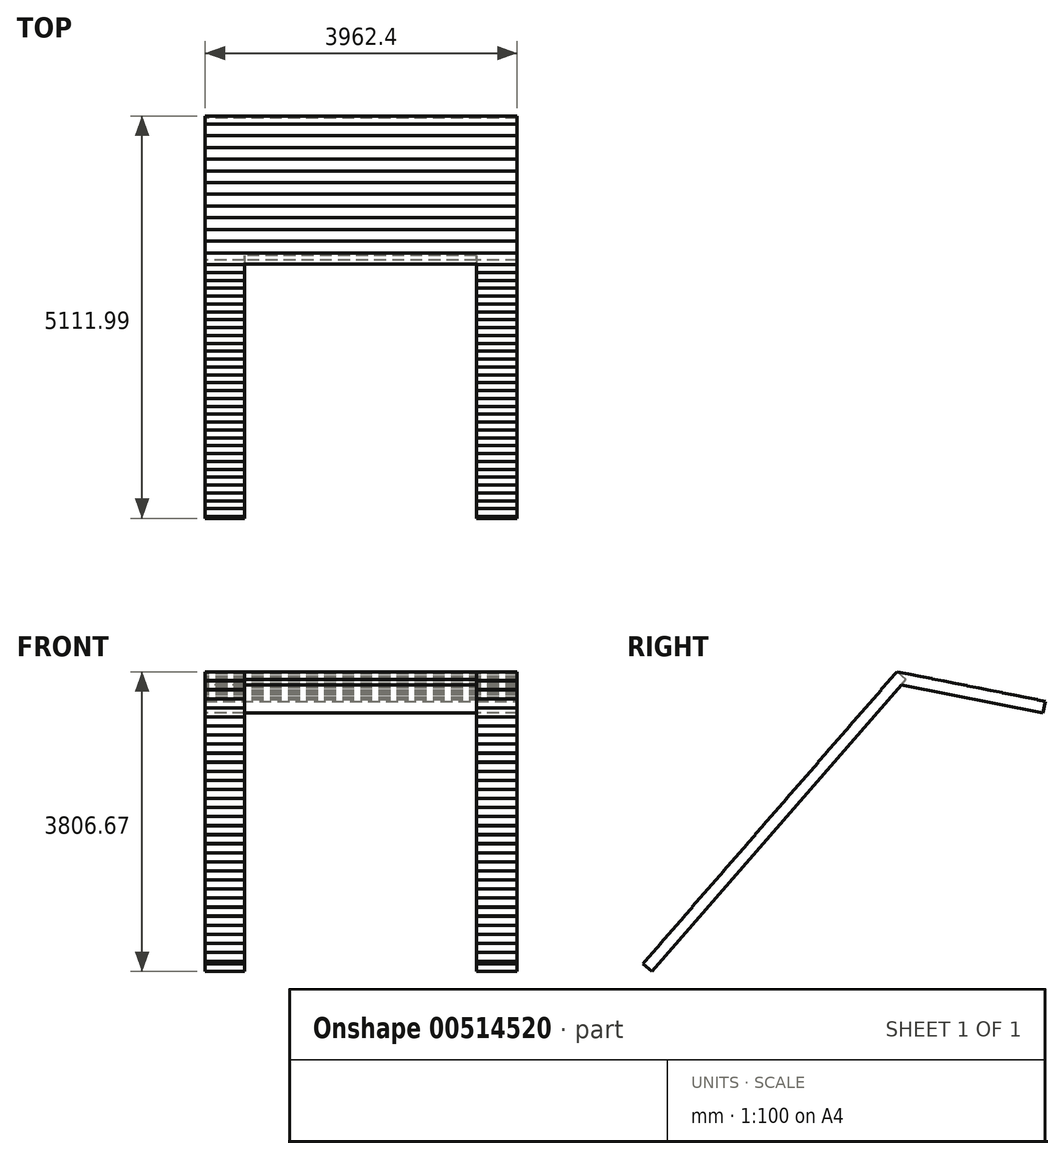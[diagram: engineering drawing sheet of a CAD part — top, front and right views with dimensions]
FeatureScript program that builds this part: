
annotation { "Feature Type Name" : "Feature", "Feature Type Description" : "" }
export const myFeature = defineFeature(function(context is Context, id is Id, definition is map)
    precondition{}
    {
        {
            var Q0;
            Q0=qCreatedBy(makeId("Right.planeOp"),FACE);
            var sketch = newSketch(context, id + "F0", { "sketchPlane" : qUnion([Q0])});
            skLineSegment(sketch, "E0", {"start": v(0, 0) * mm, "end": v(-3165.74, -3641.76) * mm});
            skLineSegment(sketch, "E1", {"start": v(0, 0) * mm, "end": v(1800.88, -359.13) * mm});
            skLineSegment(sketch, "E2", {"start": v(-1062.72, -1222.52) * mm, "end": v(-1062.72, -2262.24) * mm});
            skLineSegment(sketch, "E3", {"start": v(1800.88, -359.13) * mm, "end": v(1831.04, -207.93) * mm});
            skLineSegment(sketch, "E4", {"start": v(1831.04, -207.93) * mm, "end": v(-57.63, 168.7) * mm});
            skLineSegment(sketch, "E5", {"start": v(-57.63, 168.7) * mm, "end": v(-3282.1, -3540.62) * mm});
            skLineSegment(sketch, "E6", {"start": v(-3282.1, -3540.62) * mm, "end": v(-3165.74, -3641.76) * mm});
            skSolve(sketch);
        }
        {
            var Q0;
            {var subQ0=sQuery(id+"F0.wireOp",EDGE,"E1");Q0=makeQuery(id+"F0.imprint","IMPRINT",FACE,{"disambiguationData":[TD([[makeQuery(id+"F0.imprint","IMPRINT",EDGE,{"derivedFrom":subQ0}),1.0]])]});}
            extrude(context, id + "F1", {"entities" : qUnion([Q0]), "depth" : 3962.4 * mm, "offsetDistance" : 25.4 * mm});
        }
        {
            var Q0;
            Q0=makeQuery(id+"F1.opExtrude","SWEPT_FACE",FACE,{"disambiguationData":[OSD([sQuery(id+"F0.wireOp",EDGE,"E5")])]});
            var sketch = newSketch(context, id + "F2", { "sketchPlane" : qUnion([Q0])});
            skLineSegment(sketch, "E7.0", {"start": v(3962.4, 89.51) * mm, "end": v(0, 89.51) * mm});
            skLineSegment(sketch, "E7.1", {"start": v(3962.4, 89.51) * mm, "end": v(3962.4, -4825.39) * mm});
            skLineSegment(sketch, "E7.2", {"start": v(0, 89.51) * mm, "end": v(0, -4825.39) * mm});
            skLineSegment(sketch, "E8", {"start": v(498.76, -4825.39) * mm, "end": v(498.76, 89.51) * mm});
            skLineSegment(sketch, "E9", {"start": v(1481.74, -4825.39) * mm, "end": v(1481.74, 89.51) * mm});
            skLineSegment(sketch, "E10", {"start": v(2464.72, -4825.39) * mm, "end": v(2464.72, 89.51) * mm});
            skLineSegment(sketch, "E11", {"start": v(3447.7, -4825.39) * mm, "end": v(3447.7, 89.51) * mm});
            skLineSegment(sketch, "E12", {"start": v(498.76, -4825.39) * mm, "end": v(498.76, -3187.09) * mm});
            skLineSegment(sketch, "E13", {"start": v(498.76, -3187.09) * mm, "end": v(498.76, -1548.79) * mm});
            skLineSegment(sketch, "E14", {"start": v(498.76, -1548.79) * mm, "end": v(498.76, 89.51) * mm});
            skLineSegment(sketch, "E15", {"start": v(498.76, -4825.39) * mm, "end": v(0, -4825.39) * mm});
            skLineSegment(sketch, "E16", {"start": v(498.76, -4825.39) * mm, "end": v(1481.74, -4825.39) * mm});
            skLineSegment(sketch, "E17", {"start": v(1481.74, -4825.39) * mm, "end": v(2464.72, -4825.39) * mm});
            skLineSegment(sketch, "E18", {"start": v(2464.72, -4825.39) * mm, "end": v(3447.7, -4825.39) * mm});
            skLineSegment(sketch, "E19", {"start": v(3447.7, -4825.39) * mm, "end": v(3962.4, -4825.39) * mm});
            skPoint(sketch, "E20.orphan", {"position": v(3962.4, -4825.39) * mm});
            skLineSegment(sketch, "E21", {"start": v(498.76, 89.51) * mm, "end": v(3447.7, 89.51) * mm});
            skLineSegment(sketch, "E22", {"start": v(3447.7, 89.51) * mm, "end": v(3447.7, -4825.39) * mm});
            skLineSegment(sketch, "E23", {"start": v(3447.7, -4825.39) * mm, "end": v(498.76, -4825.39) * mm});
            skSolve(sketch);
        }
        {
            var Q0;
            {var subQ0=sQuery(id+"F2.wireOp",EDGE,"E9");Q0=makeQuery(id+"F2.imprint","IMPRINT",FACE,{"disambiguationData":[TD([[makeQuery(id+"F2.imprint","IMPRINT",EDGE,{"derivedFrom":subQ0}),1.0]])]});}
            var Q1;
            {var subQ0=sQuery(id+"F2.wireOp",EDGE,"E9");Q1=makeQuery(id+"F2.imprint","IMPRINT",FACE,{"disambiguationData":[TD([[makeQuery(id+"F2.imprint","IMPRINT",EDGE,{"derivedFrom":subQ0}),-1.0]])]});}
            var Q2;
            {var subQ0=sQuery(id+"F2.wireOp",EDGE,"E10");Q2=makeQuery(id+"F2.imprint","IMPRINT",FACE,{"disambiguationData":[TD([[makeQuery(id+"F2.imprint","IMPRINT",EDGE,{"derivedFrom":subQ0}),-1.0]])]});}
            extrude(context, id + "F3", {"entities" : qUnion([Q0, Q1, Q2]), "operationType" : NewBodyOperationType.REMOVE, "oppositeDirection" : true, "depth" : 154.18 * mm, "offsetDistance" : 25.4 * mm});
        }
        {
            var Q0;
            Q0=makeQuery(id+"F1.opExtrude","CAP_FACE",FACE,{"disambiguationData":[OSD([sQuery(id+"F0.wireOp",EDGE,"E0"),sQuery(id+"F0.wireOp",EDGE,"E1"),sQuery(id+"F0.wireOp",EDGE,"E3"),sQuery(id+"F0.wireOp",EDGE,"E4"),sQuery(id+"F0.wireOp",EDGE,"E5"),sQuery(id+"F0.wireOp",EDGE,"E6")])],"isStart":true});
            var sketch = newSketch(context, id + "F4", { "sketchPlane" : qUnion([Q0])});
            skLineSegment(sketch, "E24", {"start": v(57.63, 168.7) * mm, "end": v(157.62, 53.69) * mm});
            skLineSegment(sketch, "E25", {"start": v(157.62, 53.69) * mm, "end": v(155.7, 52.02) * mm});
            skLineSegment(sketch, "E26", {"start": v(155.7, 52.02) * mm, "end": v(257.6, -61.33) * mm});
            skLineSegment(sketch, "E27", {"start": v(255.68, -63) * mm, "end": v(257.6, -61.33) * mm});
            skLineSegment(sketch, "E28", {"start": v(255.68, -63) * mm, "end": v(357.58, -176.35) * mm});
            skLineSegment(sketch, "E29", {"start": v(357.58, -176.35) * mm, "end": v(355.7, -178.04) * mm});
            skLineSegment(sketch, "E30", {"start": v(355.7, -178.04) * mm, "end": v(457.6, -291.4) * mm});
            skLineSegment(sketch, "E31", {"start": v(457.6, -291.4) * mm, "end": v(455.7, -293.1) * mm});
            skLineSegment(sketch, "E32", {"start": v(455.7, -293.1) * mm, "end": v(557.6, -406.45) * mm});
            skLineSegment(sketch, "E33", {"start": v(557.6, -406.45) * mm, "end": v(555.72, -408.14) * mm});
            skLineSegment(sketch, "E34", {"start": v(555.72, -408.14) * mm, "end": v(657.62, -521.5) * mm});
            skLineSegment(sketch, "E35", {"start": v(657.62, -521.5) * mm, "end": v(655.73, -523.2) * mm});
            skLineSegment(sketch, "E36", {"start": v(655.73, -523.2) * mm, "end": v(757.63, -636.54) * mm});
            skLineSegment(sketch, "E37", {"start": v(757.63, -636.54) * mm, "end": v(755.74, -638.24) * mm});
            skLineSegment(sketch, "E38", {"start": v(755.74, -638.24) * mm, "end": v(857.64, -751.6) * mm});
            skLineSegment(sketch, "E39", {"start": v(857.64, -751.6) * mm, "end": v(855.75, -753.3) * mm});
            skLineSegment(sketch, "E40", {"start": v(855.75, -753.3) * mm, "end": v(957.65, -866.64) * mm});
            skLineSegment(sketch, "E41", {"start": v(957.65, -866.64) * mm, "end": v(955.76, -868.34) * mm});
            skLineSegment(sketch, "E42", {"start": v(955.76, -868.34) * mm, "end": v(1057.66, -981.7) * mm});
            skLineSegment(sketch, "E43", {"start": v(1057.66, -981.7) * mm, "end": v(1055.77, -983.4) * mm});
            skLineSegment(sketch, "E44", {"start": v(1055.77, -983.4) * mm, "end": v(1157.67, -1096.74) * mm});
            skLineSegment(sketch, "E45", {"start": v(1157.67, -1096.74) * mm, "end": v(1155.78, -1098.44) * mm});
            skLineSegment(sketch, "E46", {"start": v(1155.78, -1098.44) * mm, "end": v(1257.68, -1211.8) * mm});
            skLineSegment(sketch, "E47", {"start": v(157.62, 53.69) * mm, "end": v(57.63, 164.9) * mm});
            skLineSegment(sketch, "E48", {"start": v(57.63, 168.7) * mm, "end": v(57.63, 164.9) * mm});
            skLineSegment(sketch, "E49", {"start": v(1257.68, -1211.8) * mm, "end": v(1255.8, -1213.5) * mm});
            skLineSegment(sketch, "E50", {"start": v(1255.8, -1213.5) * mm, "end": v(1357.7, -1326.84) * mm});
            skLineSegment(sketch, "E51", {"start": v(1357.7, -1326.84) * mm, "end": v(1355.8, -1328.54) * mm});
            skLineSegment(sketch, "E52", {"start": v(1355.8, -1328.54) * mm, "end": v(1457.7, -1441.9) * mm});
            skLineSegment(sketch, "E53", {"start": v(1457.7, -1441.9) * mm, "end": v(1455.82, -1443.6) * mm});
            skLineSegment(sketch, "E54", {"start": v(1455.82, -1443.6) * mm, "end": v(1557.72, -1556.94) * mm});
            skLineSegment(sketch, "E55", {"start": v(1557.72, -1556.94) * mm, "end": v(1555.83, -1558.64) * mm});
            skLineSegment(sketch, "E56", {"start": v(1555.83, -1558.64) * mm, "end": v(1657.73, -1672) * mm});
            skLineSegment(sketch, "E57", {"start": v(1657.73, -1672) * mm, "end": v(1655.84, -1673.7) * mm});
            skLineSegment(sketch, "E58", {"start": v(1655.84, -1673.7) * mm, "end": v(1757.74, -1787.04) * mm});
            skLineSegment(sketch, "E59", {"start": v(1757.74, -1787.04) * mm, "end": v(1755.85, -1788.74) * mm});
            skLineSegment(sketch, "E60", {"start": v(1755.85, -1788.74) * mm, "end": v(1857.75, -1902.1) * mm});
            skLineSegment(sketch, "E61", {"start": v(1857.75, -1902.1) * mm, "end": v(1855.86, -1903.79) * mm});
            skLineSegment(sketch, "E62", {"start": v(1855.86, -1903.79) * mm, "end": v(1957.76, -2017.14) * mm});
            skLineSegment(sketch, "E63", {"start": v(1957.76, -2017.14) * mm, "end": v(1955.87, -2018.84) * mm});
            skLineSegment(sketch, "E64", {"start": v(1955.87, -2018.84) * mm, "end": v(2057.77, -2132.2) * mm});
            skLineSegment(sketch, "E65", {"start": v(2057.77, -2132.2) * mm, "end": v(2055.88, -2133.89) * mm});
            skLineSegment(sketch, "E66", {"start": v(2055.88, -2133.89) * mm, "end": v(2157.78, -2247.24) * mm});
            skLineSegment(sketch, "E67", {"start": v(2157.78, -2247.24) * mm, "end": v(2155.9, -2248.94) * mm});
            skLineSegment(sketch, "E68", {"start": v(2155.9, -2248.94) * mm, "end": v(2257.8, -2362.3) * mm});
            skLineSegment(sketch, "E69", {"start": v(2257.8, -2362.3) * mm, "end": v(2255.9, -2363.99) * mm});
            skLineSegment(sketch, "E70", {"start": v(2255.9, -2363.99) * mm, "end": v(2357.8, -2477.34) * mm});
            skLineSegment(sketch, "E71", {"start": v(2357.8, -2477.34) * mm, "end": v(2355.92, -2479.04) * mm});
            skLineSegment(sketch, "E72", {"start": v(2355.92, -2479.04) * mm, "end": v(2457.82, -2592.39) * mm});
            skLineSegment(sketch, "E73", {"start": v(2457.82, -2592.39) * mm, "end": v(2455.93, -2594.09) * mm});
            skLineSegment(sketch, "E74", {"start": v(2455.93, -2594.09) * mm, "end": v(2557.83, -2707.44) * mm});
            skLineSegment(sketch, "E75", {"start": v(2557.83, -2707.44) * mm, "end": v(2555.94, -2709.14) * mm});
            skLineSegment(sketch, "E76", {"start": v(2555.94, -2709.14) * mm, "end": v(2657.84, -2822.49) * mm});
            skLineSegment(sketch, "E77", {"start": v(2657.84, -2822.49) * mm, "end": v(2655.95, -2824.19) * mm});
            skLineSegment(sketch, "E78", {"start": v(2655.95, -2824.19) * mm, "end": v(2757.85, -2937.54) * mm});
            skLineSegment(sketch, "E79", {"start": v(2757.85, -2937.54) * mm, "end": v(2755.96, -2939.24) * mm});
            skLineSegment(sketch, "E80", {"start": v(2755.96, -2939.24) * mm, "end": v(2857.86, -3052.59) * mm});
            skLineSegment(sketch, "E81", {"start": v(2857.86, -3052.59) * mm, "end": v(2855.97, -3054.29) * mm});
            skLineSegment(sketch, "E82", {"start": v(2855.97, -3054.29) * mm, "end": v(2957.87, -3167.64) * mm});
            skLineSegment(sketch, "E83", {"start": v(2957.87, -3167.64) * mm, "end": v(2955.98, -3169.34) * mm});
            skLineSegment(sketch, "E84", {"start": v(2955.98, -3169.34) * mm, "end": v(3057.88, -3282.69) * mm});
            skLineSegment(sketch, "E85", {"start": v(3057.88, -3282.69) * mm, "end": v(3056, -3284.39) * mm});
            skLineSegment(sketch, "E86", {"start": v(3056, -3284.39) * mm, "end": v(3157.9, -3397.74) * mm});
            skLineSegment(sketch, "E87", {"start": v(3157.9, -3397.74) * mm, "end": v(3156, -3399.44) * mm});
            skLineSegment(sketch, "E88", {"start": v(3156, -3399.44) * mm, "end": v(3257.9, -3512.79) * mm});
            skLineSegment(sketch, "E89", {"start": v(3257.9, -3512.79) * mm, "end": v(3256.02, -3514.49) * mm});
            skLineSegment(sketch, "E90", {"start": v(3256.02, -3514.49) * mm, "end": v(3359.8, -3626.12) * mm});
            skLineSegment(sketch, "E91", {"start": v(3257.9, -3512.79) * mm, "end": v(3359.8, -3626.12) * mm});
            skLineSegment(sketch, "E92", {"start": v(57.63, 168.7) * mm, "end": v(-91.82, 138.9) * mm});
            skLineSegment(sketch, "E93", {"start": v(-91.82, 138.9) * mm, "end": v(57.63, 164.9) * mm});
            skLineSegment(sketch, "E94", {"start": v(-91.82, 138.9) * mm, "end": v(-91.33, 136.41) * mm});
            skLineSegment(sketch, "E95", {"start": v(-91.33, 136.41) * mm, "end": v(-240.58, 109.24) * mm});
            skLineSegment(sketch, "E96", {"start": v(-240.58, 109.24) * mm, "end": v(-240.12, 106.74) * mm});
            skLineSegment(sketch, "E97", {"start": v(-240.12, 106.74) * mm, "end": v(-389.37, 79.57) * mm});
            skLineSegment(sketch, "E98", {"start": v(-389.37, 79.57) * mm, "end": v(-388.92, 77.07) * mm});
            skLineSegment(sketch, "E99", {"start": v(-388.92, 77.07) * mm, "end": v(-538.16, 49.9) * mm});
            skLineSegment(sketch, "E100", {"start": v(-538.16, 49.9) * mm, "end": v(-537.7, 47.4) * mm});
            skLineSegment(sketch, "E101", {"start": v(-537.7, 47.4) * mm, "end": v(-686.96, 20.22) * mm});
            skLineSegment(sketch, "E102", {"start": v(-686.96, 20.22) * mm, "end": v(-686.5, 17.72) * mm});
            skLineSegment(sketch, "E103", {"start": v(-686.5, 17.72) * mm, "end": v(-835.75, -9.45) * mm});
            skLineSegment(sketch, "E104", {"start": v(-835.75, -9.45) * mm, "end": v(-835.3, -11.95) * mm});
            skLineSegment(sketch, "E105", {"start": v(-835.3, -11.95) * mm, "end": v(-984.55, -39.13) * mm});
            skLineSegment(sketch, "E106", {"start": v(-984.55, -39.13) * mm, "end": v(-984.1, -41.62) * mm});
            skLineSegment(sketch, "E107", {"start": v(-984.1, -41.62) * mm, "end": v(-1133.34, -68.8) * mm});
            skLineSegment(sketch, "E108", {"start": v(-1133.34, -68.8) * mm, "end": v(-1132.89, -71.3) * mm});
            skLineSegment(sketch, "E109", {"start": v(-1132.89, -71.3) * mm, "end": v(-1282.14, -98.47) * mm});
            skLineSegment(sketch, "E110", {"start": v(-1282.14, -98.47) * mm, "end": v(-1281.68, -100.97) * mm});
            skLineSegment(sketch, "E111", {"start": v(-1281.68, -100.97) * mm, "end": v(-1430.93, -128.14) * mm});
            skLineSegment(sketch, "E112", {"start": v(-1430.93, -128.14) * mm, "end": v(-1430.48, -130.64) * mm});
            skLineSegment(sketch, "E113", {"start": v(-1430.48, -130.64) * mm, "end": v(-1579.72, -157.82) * mm});
            skLineSegment(sketch, "E114", {"start": v(-1579.72, -157.82) * mm, "end": v(-1579.27, -160.31) * mm});
            skLineSegment(sketch, "E115", {"start": v(-1579.27, -160.31) * mm, "end": v(-1728.52, -187.49) * mm});
            skLineSegment(sketch, "E116", {"start": v(-1728.52, -187.49) * mm, "end": v(-1728.06, -189.99) * mm});
            skLineSegment(sketch, "E117", {"start": v(-1728.52, -187.49) * mm, "end": v(-1877.98, -217.3) * mm});
            skLineSegment(sketch, "E118", {"start": v(-1877.98, -217.3) * mm, "end": v(-1728.06, -189.99) * mm});
            skSolve(sketch);
        }
        {
            var Q0;
            Q0 = qSketchRegion(id + "F4", true);
            var Q1;
            {var subQ0=sQuery(id+"F4.wireOp",EDGE,"E25");Q1=makeQuery(id+"F4.imprint","IMPRINT",FACE,{"disambiguationData":[TD([[makeQuery(id+"F4.imprint","IMPRINT",EDGE,{"derivedFrom":subQ0}),1.0]])]});}
            var Q2;
            {var subQ0=sQuery(id+"F4.wireOp",EDGE,"E27");Q2=makeQuery(id+"F4.imprint","IMPRINT",FACE,{"disambiguationData":[TD([[makeQuery(id+"F4.imprint","IMPRINT",EDGE,{"derivedFrom":subQ0}),-1.0]])]});}
            var Q3;
            {var subQ0=sQuery(id+"F4.wireOp",EDGE,"E29");Q3=makeQuery(id+"F4.imprint","IMPRINT",FACE,{"disambiguationData":[TD([[makeQuery(id+"F4.imprint","IMPRINT",EDGE,{"derivedFrom":subQ0}),1.0]])]});}
            var Q4;
            {var subQ0=sQuery(id+"F4.wireOp",EDGE,"E31");Q4=makeQuery(id+"F4.imprint","IMPRINT",FACE,{"disambiguationData":[TD([[makeQuery(id+"F4.imprint","IMPRINT",EDGE,{"derivedFrom":subQ0}),1.0]])]});}
            var Q5;
            {var subQ0=sQuery(id+"F4.wireOp",EDGE,"E33");Q5=makeQuery(id+"F4.imprint","IMPRINT",FACE,{"disambiguationData":[TD([[makeQuery(id+"F4.imprint","IMPRINT",EDGE,{"derivedFrom":subQ0}),1.0]])]});}
            var Q6;
            {var subQ0=sQuery(id+"F4.wireOp",EDGE,"E35");Q6=makeQuery(id+"F4.imprint","IMPRINT",FACE,{"disambiguationData":[TD([[makeQuery(id+"F4.imprint","IMPRINT",EDGE,{"derivedFrom":subQ0}),1.0]])]});}
            var Q7;
            {var subQ0=sQuery(id+"F4.wireOp",EDGE,"E37");Q7=makeQuery(id+"F4.imprint","IMPRINT",FACE,{"disambiguationData":[TD([[makeQuery(id+"F4.imprint","IMPRINT",EDGE,{"derivedFrom":subQ0}),1.0]])]});}
            var Q8;
            {var subQ0=sQuery(id+"F4.wireOp",EDGE,"E39");Q8=makeQuery(id+"F4.imprint","IMPRINT",FACE,{"disambiguationData":[TD([[makeQuery(id+"F4.imprint","IMPRINT",EDGE,{"derivedFrom":subQ0}),1.0]])]});}
            var Q9;
            {var subQ0=sQuery(id+"F4.wireOp",EDGE,"E41");Q9=makeQuery(id+"F4.imprint","IMPRINT",FACE,{"disambiguationData":[TD([[makeQuery(id+"F4.imprint","IMPRINT",EDGE,{"derivedFrom":subQ0}),1.0]])]});}
            var Q10;
            {var subQ0=sQuery(id+"F4.wireOp",EDGE,"E43");Q10=makeQuery(id+"F4.imprint","IMPRINT",FACE,{"disambiguationData":[TD([[makeQuery(id+"F4.imprint","IMPRINT",EDGE,{"derivedFrom":subQ0}),1.0]])]});}
            var Q11;
            {var subQ0=sQuery(id+"F4.wireOp",EDGE,"E45");Q11=makeQuery(id+"F4.imprint","IMPRINT",FACE,{"disambiguationData":[TD([[makeQuery(id+"F4.imprint","IMPRINT",EDGE,{"derivedFrom":subQ0}),1.0]])]});}
            var Q12;
            {var subQ0=sQuery(id+"F4.wireOp",EDGE,"E49");Q12=makeQuery(id+"F4.imprint","IMPRINT",FACE,{"disambiguationData":[TD([[makeQuery(id+"F4.imprint","IMPRINT",EDGE,{"derivedFrom":subQ0}),1.0]])]});}
            var Q13;
            {var subQ0=sQuery(id+"F4.wireOp",EDGE,"E51");Q13=makeQuery(id+"F4.imprint","IMPRINT",FACE,{"disambiguationData":[TD([[makeQuery(id+"F4.imprint","IMPRINT",EDGE,{"derivedFrom":subQ0}),1.0]])]});}
            var Q14;
            {var subQ0=sQuery(id+"F4.wireOp",EDGE,"E53");Q14=makeQuery(id+"F4.imprint","IMPRINT",FACE,{"disambiguationData":[TD([[makeQuery(id+"F4.imprint","IMPRINT",EDGE,{"derivedFrom":subQ0}),1.0]])]});}
            var Q15;
            {var subQ0=sQuery(id+"F4.wireOp",EDGE,"E55");Q15=makeQuery(id+"F4.imprint","IMPRINT",FACE,{"disambiguationData":[TD([[makeQuery(id+"F4.imprint","IMPRINT",EDGE,{"derivedFrom":subQ0}),1.0]])]});}
            var Q16;
            {var subQ0=sQuery(id+"F4.wireOp",EDGE,"E61");Q16=makeQuery(id+"F4.imprint","IMPRINT",FACE,{"disambiguationData":[TD([[makeQuery(id+"F4.imprint","IMPRINT",EDGE,{"derivedFrom":subQ0}),1.0]])]});}
            var Q17;
            {var subQ0=sQuery(id+"F4.wireOp",EDGE,"E59");Q17=makeQuery(id+"F4.imprint","IMPRINT",FACE,{"disambiguationData":[TD([[makeQuery(id+"F4.imprint","IMPRINT",EDGE,{"derivedFrom":subQ0}),1.0]])]});}
            var Q18;
            {var subQ0=sQuery(id+"F4.wireOp",EDGE,"E57");Q18=makeQuery(id+"F4.imprint","IMPRINT",FACE,{"disambiguationData":[TD([[makeQuery(id+"F4.imprint","IMPRINT",EDGE,{"derivedFrom":subQ0}),1.0]])]});}
            var Q19;
            {var subQ0=sQuery(id+"F4.wireOp",EDGE,"E63");Q19=makeQuery(id+"F4.imprint","IMPRINT",FACE,{"disambiguationData":[TD([[makeQuery(id+"F4.imprint","IMPRINT",EDGE,{"derivedFrom":subQ0}),1.0]])]});}
            var Q20;
            {var subQ0=sQuery(id+"F4.wireOp",EDGE,"E65");Q20=makeQuery(id+"F4.imprint","IMPRINT",FACE,{"disambiguationData":[TD([[makeQuery(id+"F4.imprint","IMPRINT",EDGE,{"derivedFrom":subQ0}),1.0]])]});}
            var Q21;
            {var subQ0=sQuery(id+"F4.wireOp",EDGE,"E67");Q21=makeQuery(id+"F4.imprint","IMPRINT",FACE,{"disambiguationData":[TD([[makeQuery(id+"F4.imprint","IMPRINT",EDGE,{"derivedFrom":subQ0}),1.0]])]});}
            var Q22;
            {var subQ0=sQuery(id+"F4.wireOp",EDGE,"E69");Q22=makeQuery(id+"F4.imprint","IMPRINT",FACE,{"disambiguationData":[TD([[makeQuery(id+"F4.imprint","IMPRINT",EDGE,{"derivedFrom":subQ0}),1.0]])]});}
            var Q23;
            {var subQ0=sQuery(id+"F4.wireOp",EDGE,"E71");Q23=makeQuery(id+"F4.imprint","IMPRINT",FACE,{"disambiguationData":[TD([[makeQuery(id+"F4.imprint","IMPRINT",EDGE,{"derivedFrom":subQ0}),1.0]])]});}
            var Q24;
            {var subQ0=sQuery(id+"F4.wireOp",EDGE,"E73");Q24=makeQuery(id+"F4.imprint","IMPRINT",FACE,{"disambiguationData":[TD([[makeQuery(id+"F4.imprint","IMPRINT",EDGE,{"derivedFrom":subQ0}),1.0]])]});}
            var Q25;
            {var subQ0=sQuery(id+"F4.wireOp",EDGE,"E75");Q25=makeQuery(id+"F4.imprint","IMPRINT",FACE,{"disambiguationData":[TD([[makeQuery(id+"F4.imprint","IMPRINT",EDGE,{"derivedFrom":subQ0}),1.0]])]});}
            var Q26;
            {var subQ0=sQuery(id+"F4.wireOp",EDGE,"E77");Q26=makeQuery(id+"F4.imprint","IMPRINT",FACE,{"disambiguationData":[TD([[makeQuery(id+"F4.imprint","IMPRINT",EDGE,{"derivedFrom":subQ0}),1.0]])]});}
            var Q27;
            {var subQ0=sQuery(id+"F4.wireOp",EDGE,"E79");Q27=makeQuery(id+"F4.imprint","IMPRINT",FACE,{"disambiguationData":[TD([[makeQuery(id+"F4.imprint","IMPRINT",EDGE,{"derivedFrom":subQ0}),1.0]])]});}
            var Q28;
            {var subQ0=sQuery(id+"F4.wireOp",EDGE,"E81");Q28=makeQuery(id+"F4.imprint","IMPRINT",FACE,{"disambiguationData":[TD([[makeQuery(id+"F4.imprint","IMPRINT",EDGE,{"derivedFrom":subQ0}),1.0]])]});}
            var Q29;
            {var subQ0=sQuery(id+"F4.wireOp",EDGE,"E83");Q29=makeQuery(id+"F4.imprint","IMPRINT",FACE,{"disambiguationData":[TD([[makeQuery(id+"F4.imprint","IMPRINT",EDGE,{"derivedFrom":subQ0}),1.0]])]});}
            var Q30;
            {var subQ0=sQuery(id+"F4.wireOp",EDGE,"E85");Q30=makeQuery(id+"F4.imprint","IMPRINT",FACE,{"disambiguationData":[TD([[makeQuery(id+"F4.imprint","IMPRINT",EDGE,{"derivedFrom":subQ0}),1.0]])]});}
            var Q31;
            {var subQ0=sQuery(id+"F4.wireOp",EDGE,"E87");Q31=makeQuery(id+"F4.imprint","IMPRINT",FACE,{"disambiguationData":[TD([[makeQuery(id+"F4.imprint","IMPRINT",EDGE,{"derivedFrom":subQ0}),1.0]])]});}
            var Q32;
            {var subQ0=sQuery(id+"F4.wireOp",EDGE,"E114");Q32=makeQuery(id+"F4.imprint","IMPRINT",FACE,{"disambiguationData":[TD([[makeQuery(id+"F4.imprint","IMPRINT",EDGE,{"derivedFrom":subQ0}),-1.0]])]});}
            var Q33;
            {var subQ0=sQuery(id+"F4.wireOp",EDGE,"E112");Q33=makeQuery(id+"F4.imprint","IMPRINT",FACE,{"disambiguationData":[TD([[makeQuery(id+"F4.imprint","IMPRINT",EDGE,{"derivedFrom":subQ0}),-1.0]])]});}
            var Q34;
            {var subQ0=sQuery(id+"F4.wireOp",EDGE,"E110");Q34=makeQuery(id+"F4.imprint","IMPRINT",FACE,{"disambiguationData":[TD([[makeQuery(id+"F4.imprint","IMPRINT",EDGE,{"derivedFrom":subQ0}),-1.0]])]});}
            var Q35;
            {var subQ0=sQuery(id+"F4.wireOp",EDGE,"E108");Q35=makeQuery(id+"F4.imprint","IMPRINT",FACE,{"disambiguationData":[TD([[makeQuery(id+"F4.imprint","IMPRINT",EDGE,{"derivedFrom":subQ0}),-1.0]])]});}
            var Q36;
            {var subQ0=sQuery(id+"F4.wireOp",EDGE,"E106");Q36=makeQuery(id+"F4.imprint","IMPRINT",FACE,{"disambiguationData":[TD([[makeQuery(id+"F4.imprint","IMPRINT",EDGE,{"derivedFrom":subQ0}),-1.0]])]});}
            var Q37;
            {var subQ0=sQuery(id+"F4.wireOp",EDGE,"E104");Q37=makeQuery(id+"F4.imprint","IMPRINT",FACE,{"disambiguationData":[TD([[makeQuery(id+"F4.imprint","IMPRINT",EDGE,{"derivedFrom":subQ0}),-1.0]])]});}
            var Q38;
            {var subQ0=sQuery(id+"F4.wireOp",EDGE,"E102");Q38=makeQuery(id+"F4.imprint","IMPRINT",FACE,{"disambiguationData":[TD([[makeQuery(id+"F4.imprint","IMPRINT",EDGE,{"derivedFrom":subQ0}),-1.0]])]});}
            var Q39;
            {var subQ0=sQuery(id+"F4.wireOp",EDGE,"E100");Q39=makeQuery(id+"F4.imprint","IMPRINT",FACE,{"disambiguationData":[TD([[makeQuery(id+"F4.imprint","IMPRINT",EDGE,{"derivedFrom":subQ0}),-1.0]])]});}
            var Q40;
            {var subQ0=sQuery(id+"F4.wireOp",EDGE,"E98");Q40=makeQuery(id+"F4.imprint","IMPRINT",FACE,{"disambiguationData":[TD([[makeQuery(id+"F4.imprint","IMPRINT",EDGE,{"derivedFrom":subQ0}),-1.0]])]});}
            var Q41;
            {var subQ0=sQuery(id+"F4.wireOp",EDGE,"E96");Q41=makeQuery(id+"F4.imprint","IMPRINT",FACE,{"disambiguationData":[TD([[makeQuery(id+"F4.imprint","IMPRINT",EDGE,{"derivedFrom":subQ0}),-1.0]])]});}
            var Q42;
            {var subQ0=sQuery(id+"F4.wireOp",EDGE,"E94");Q42=makeQuery(id+"F4.imprint","IMPRINT",FACE,{"disambiguationData":[TD([[makeQuery(id+"F4.imprint","IMPRINT",EDGE,{"derivedFrom":subQ0}),-1.0]])]});}
            extrude(context, id + "F5", {"entities" : qUnion([Q0, Q1, Q2, Q3, Q4, Q5, Q6, Q7, Q8, Q9, Q10, Q11, Q12, Q13, Q14, Q15, Q16, Q17, Q18, Q19, Q20, Q21, Q22, Q23, Q24, Q25, Q26, Q27, Q28, Q29, Q30, Q31, Q32, Q33, Q34, Q35, Q36, Q37, Q38, Q39, Q40, Q41, Q42]), "operationType" : NewBodyOperationType.REMOVE, "oppositeDirection" : true, "depth" : 3962.4 * mm, "offsetDistance" : 25.4 * mm});
        }
    });
